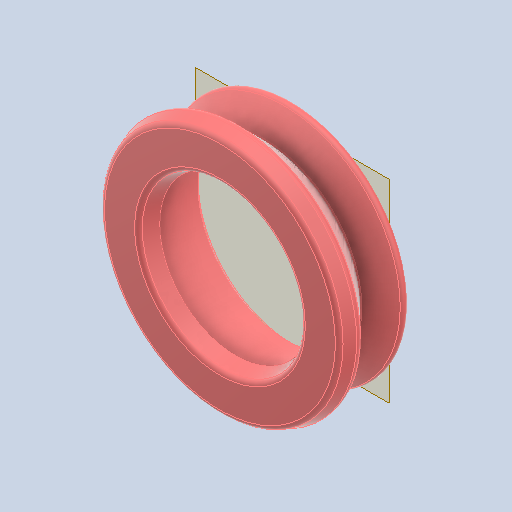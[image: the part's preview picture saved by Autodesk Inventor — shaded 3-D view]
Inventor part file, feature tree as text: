
AUTODESK INVENTOR PART (.ipt)
format: ipt  version: 2022 (Build 260153000, 153)  size: 211,968 bytes
history: native  units: in
note: dims shown in document units (in); Inventor stores cm internally (conversion verified against a paired STEP export)
features: other x3, sketch x1, plane x1
ambient origin geometry x8: Origin, YZ Plane, XZ Plane, XY Plane, X Axis, Y Axis, Z Axis, Center Point
bodies: Solid1 (feature_tree)
feature tree (5):
  other  "vroller.ipt"
  other  "Solid1::vroller.ipt"
  other  "TaggingFeature1"
  sketch  "Sketch1"  dims[d0=0.3937in]
  plane  "Work Plane1"
